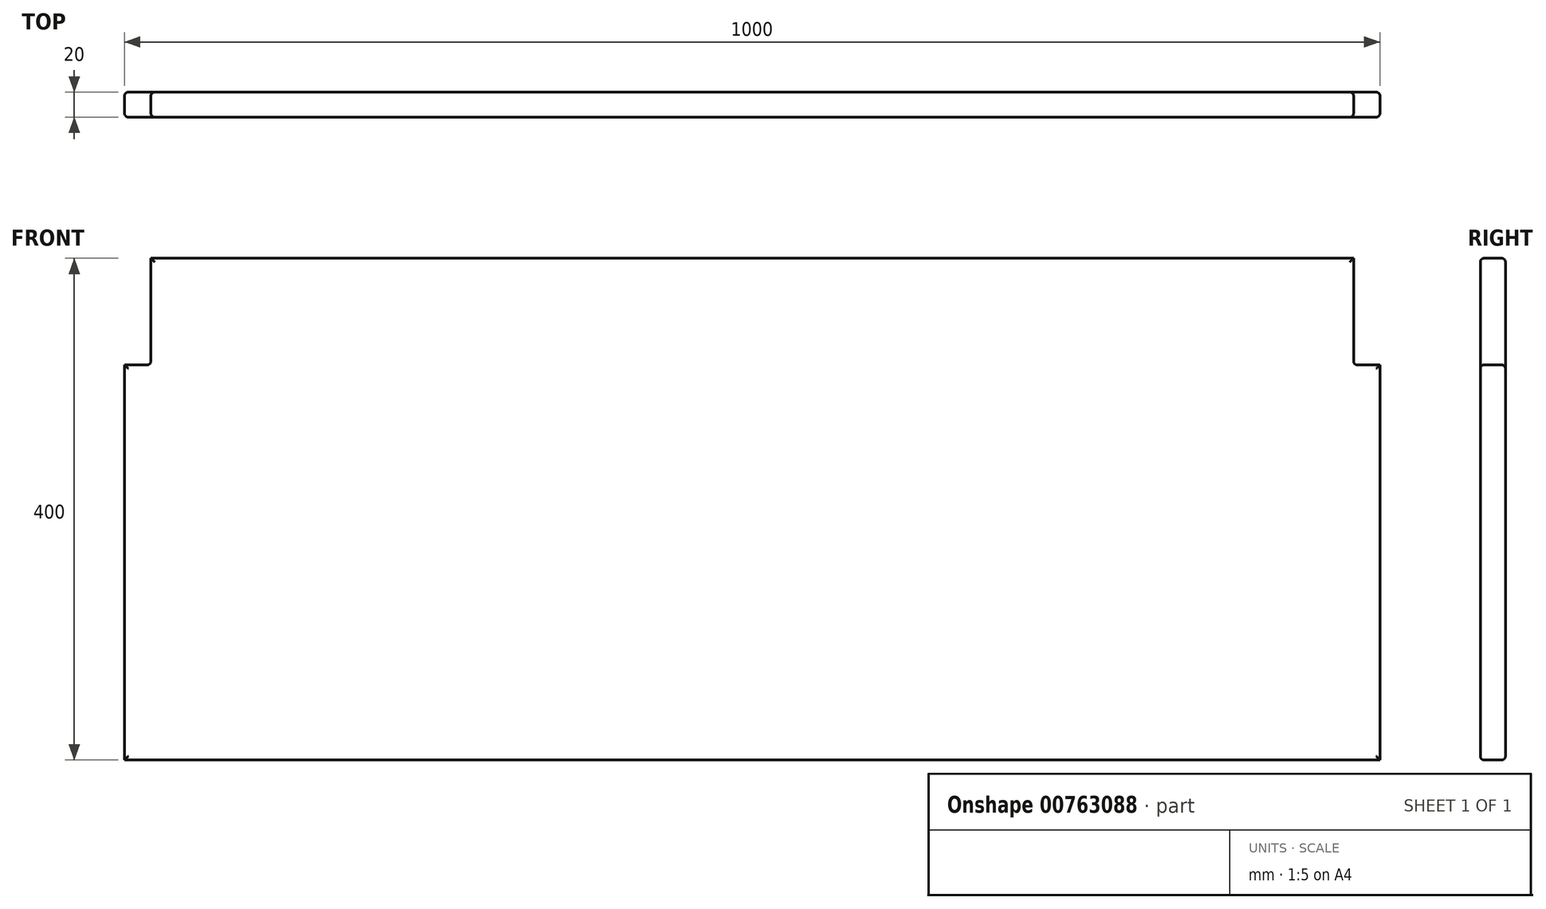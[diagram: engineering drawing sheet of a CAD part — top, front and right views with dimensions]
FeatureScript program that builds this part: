
annotation { "Feature Type Name" : "Feature", "Feature Type Description" : "" }
export const myFeature = defineFeature(function(context is Context, id is Id, definition is map)
    precondition{}
    {
        {
            var Q0;
            Q0=qCreatedBy(makeId("Front.planeOp"),FACE);
            var sketch = newSketch(context, id + "F0", { "sketchPlane" : qUnion([Q0])});
            skLineSegment(sketch, "E0.bottom", {"start": v(0, 0) * mm, "end": v(1000, 0) * mm});
            skLineSegment(sketch, "E0.top", {"start": v(21, 400) * mm, "end": v(979, 400) * mm});
            skLineSegment(sketch, "E0.left", {"start": v(0, 0) * mm, "end": v(0, 315) * mm});
            skLineSegment(sketch, "E0.right", {"start": v(1000, 0) * mm, "end": v(1000, 315) * mm});
            skLineSegment(sketch, "E1.top", {"start": v(1000, 315) * mm, "end": v(979, 315) * mm});
            skLineSegment(sketch, "E1.right", {"start": v(979, 400) * mm, "end": v(979, 315) * mm});
            skLineSegment(sketch, "E2.MirrorCS", {"start": v(0, 315) * mm, "end": v(21, 315) * mm});
            skLineSegment(sketch, "E3.MirrorCS", {"start": v(21, 400) * mm, "end": v(21, 315) * mm});
            skSolve(sketch);
        }
        {
            var Q0;
            Q0=makeQuery(id+"F0.imprint","IMPRINT",FACE,{"disambiguationData":[TD([[makeQuery(id+"F0.imprint","IMPRINT",EDGE,{"derivedFrom":sQuery(id+"F0.wireOp",EDGE,"E0.bottom")}),1.0]])]});
            extrude(context, id + "F1", {"entities" : qUnion([Q0]), "depth" : 20 * mm, "offsetDistance" : 25 * mm});
        }
        {
            var Q0;
            Q0=makeQuery(id+"F1.opExtrude","CAP_FACE",FACE,{"disambiguationData":[OSD([sQuery(id+"F0.wireOp",EDGE,"E0.bottom"),sQuery(id+"F0.wireOp",EDGE,"E0.top"),sQuery(id+"F0.wireOp",EDGE,"E0.left"),sQuery(id+"F0.wireOp",EDGE,"E0.right"),sQuery(id+"F0.wireOp",EDGE,"E1.top"),sQuery(id+"F0.wireOp",EDGE,"E1.right"),sQuery(id+"F0.wireOp",EDGE,"E2.MirrorCS"),sQuery(id+"F0.wireOp",EDGE,"E3.MirrorCS")])],"isStart":false});
            var Q1;
            Q1=makeQuery(id+"F1.opExtrude","CAP_FACE",FACE,{"disambiguationData":[OSD([sQuery(id+"F0.wireOp",EDGE,"E0.bottom"),sQuery(id+"F0.wireOp",EDGE,"E0.top"),sQuery(id+"F0.wireOp",EDGE,"E0.left"),sQuery(id+"F0.wireOp",EDGE,"E0.right"),sQuery(id+"F0.wireOp",EDGE,"E1.top"),sQuery(id+"F0.wireOp",EDGE,"E1.right"),sQuery(id+"F0.wireOp",EDGE,"E2.MirrorCS"),sQuery(id+"F0.wireOp",EDGE,"E3.MirrorCS")])],"isStart":true});
            var Q2;
            Q2=makeQuery(id+"F1.opExtrude","SWEPT_EDGE",EDGE,{"disambiguationData":[OSD([sQuery(id+"F0.wireOp",EDGE,"E2.MirrorCS"),sQuery(id+"F0.wireOp",EDGE,"E3.MirrorCS")])]});
            var Q3;
            Q3=makeQuery(id+"F1.opExtrude","SWEPT_EDGE",EDGE,{"disambiguationData":[OSD([sQuery(id+"F0.wireOp",EDGE,"E1.top"),sQuery(id+"F0.wireOp",EDGE,"E1.right")])]});
            fillet(context, id + "F2", {"entities" : qUnion([Q0, Q1, Q2, Q3]), "radius" : 3 * mm, "tangentPropagation" : true, "allowEdgeOverflow" : false});
        }
        {
            var Q0;
            Q0=makeQuery(id+"F1.opExtrude","CAP_FACE",FACE,{"disambiguationData":[OSD([sQuery(id+"F0.wireOp",EDGE,"E0.bottom"),sQuery(id+"F0.wireOp",EDGE,"E0.top"),sQuery(id+"F0.wireOp",EDGE,"E0.left"),sQuery(id+"F0.wireOp",EDGE,"E0.right"),sQuery(id+"F0.wireOp",EDGE,"E1.top"),sQuery(id+"F0.wireOp",EDGE,"E1.right"),sQuery(id+"F0.wireOp",EDGE,"E2.MirrorCS"),sQuery(id+"F0.wireOp",EDGE,"E3.MirrorCS")])],"isStart":false});
            var sketch = newSketch(context, id + "F3", { "sketchPlane" : qUnion([Q0])});
            skLineSegment(sketch, "E4", {"start": v(10.5, 312) * mm, "end": v(10.5, 230) * mm});
            skLineSegment(sketch, "E5", {"start": v(989.5, 312) * mm, "end": v(989.5, 230) * mm});
            skSolve(sketch);
        }
    });
